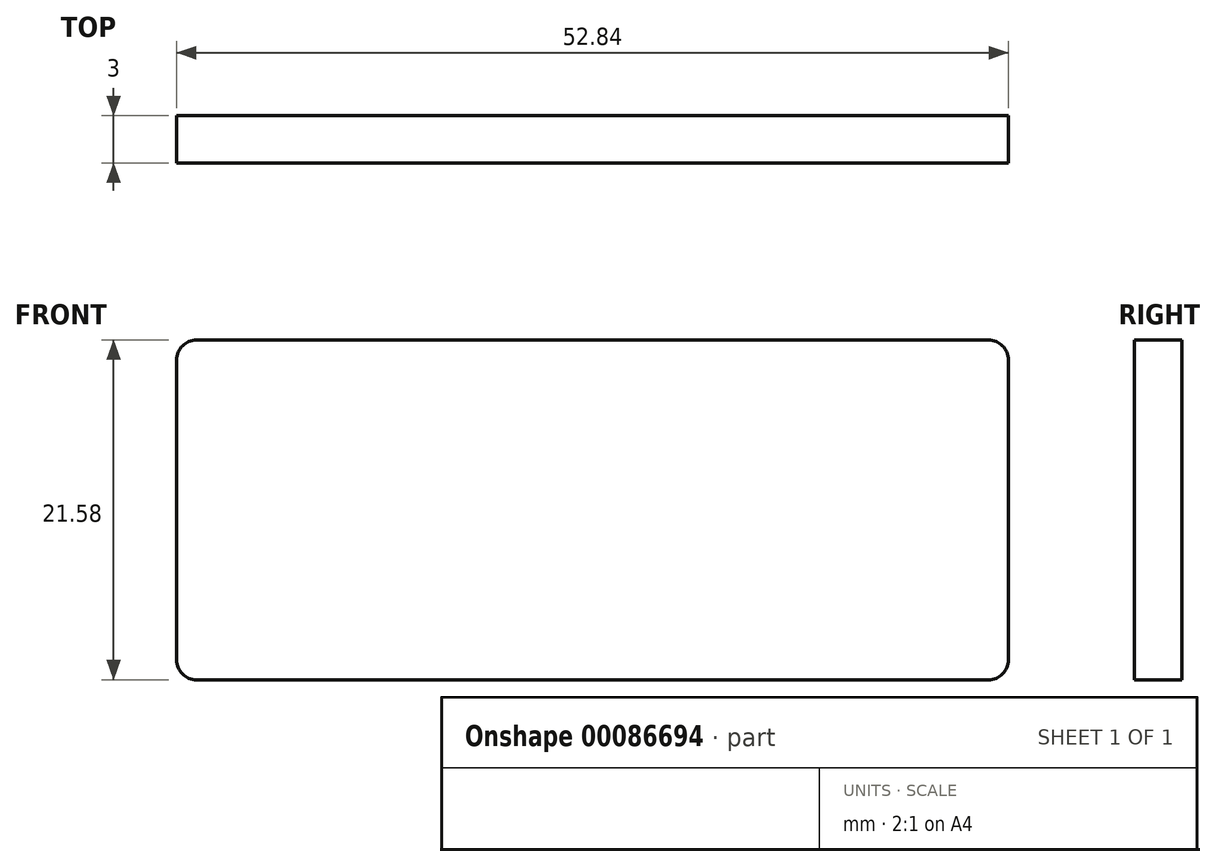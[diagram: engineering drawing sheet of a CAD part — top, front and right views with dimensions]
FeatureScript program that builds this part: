
annotation { "Feature Type Name" : "Feature", "Feature Type Description" : "" }
export const myFeature = defineFeature(function(context is Context, id is Id, definition is map)
    precondition{}
    {
        {
            var Q0;
            Q0=qCreatedBy(makeId("Front.planeOp"),FACE);
            var sketch = newSketch(context, id + "F0", { "sketchPlane" : qUnion([Q0])});
            skLineSegment(sketch, "E0.bottom", {"start": v(-25.15, 10.8) * mm, "end": v(25.15, 10.8) * mm});
            skLineSegment(sketch, "E0.top", {"start": v(-25.15, -10.8) * mm, "end": v(25.15, -10.8) * mm});
            skLineSegment(sketch, "E0.left", {"start": v(-26.42, 9.53) * mm, "end": v(-26.42, -9.53) * mm});
            skLineSegment(sketch, "E0.right", {"start": v(26.42, 9.53) * mm, "end": v(26.42, -9.53) * mm});
            skPoint(sketch, "E0.middle", {"position": v(0, 0) * mm});
            skPoint(sketch, "E1.visualSharp", {"position": v(-26.42, 10.8) * mm});
            skArc(sketch, "E1.filletArc", {"start": v(-25.15, 10.8) * mm, "mid": v(-26.04, 10.42) * mm, "end": v(-26.42, 9.53) * mm});
            skPoint(sketch, "E2.visualSharp", {"position": v(-26.42, -10.8) * mm});
            skArc(sketch, "E2.filletArc", {"start": v(-26.42, -9.53) * mm, "mid": v(-26.04, -10.42) * mm, "end": v(-25.15, -10.8) * mm});
            skPoint(sketch, "E3.visualSharp", {"position": v(26.42, 10.8) * mm});
            skArc(sketch, "E3.filletArc", {"start": v(26.42, 9.53) * mm, "mid": v(26.04, 10.42) * mm, "end": v(25.15, 10.8) * mm});
            skPoint(sketch, "E4.visualSharp", {"position": v(26.42, -10.8) * mm});
            skArc(sketch, "E4.filletArc", {"start": v(25.15, -10.8) * mm, "mid": v(26.04, -10.42) * mm, "end": v(26.42, -9.53) * mm});
            skSolve(sketch);
        }
        {
            var Q0;
            Q0=makeQuery(id+"F0.imprint","IMPRINT",FACE,{"disambiguationData":[TD([[makeQuery(id+"F0.imprint","IMPRINT",EDGE,{"derivedFrom":sQuery(id+"F0.wireOp",EDGE,"E0.bottom")}),-1.0]])]});
            extrude(context, id + "F1", {"entities" : qUnion([Q0]), "depth" : 3 * mm});
        }
    });
